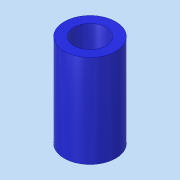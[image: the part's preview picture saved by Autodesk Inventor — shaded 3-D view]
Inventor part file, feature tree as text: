
AUTODESK INVENTOR PART (.ipt)
format: ipt  version: 2018 (Build 220112000, 112)  size: 83,968 bytes
history: native  units: mm
features: extrude x1, sketch x1
ambient origin geometry x8: Origin, YZ Plane, XZ Plane, XY Plane, X Axis, Y Axis, Z Axis, Center Point
bodies: Volumenkörper1 (feature_tree)
feature tree (2):
  extrude  "Extrusion1"  Depth=7.2mm
  sketch  "Skizze1"  dims[d0=2.5mm d1=4.0mm d2=7.2mm d3=0.0mm]
